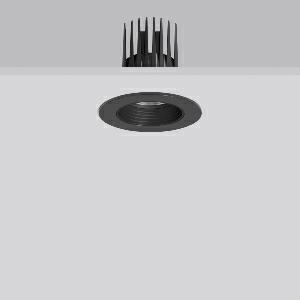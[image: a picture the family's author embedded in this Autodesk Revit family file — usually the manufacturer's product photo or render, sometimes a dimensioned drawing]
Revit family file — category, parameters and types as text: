
# Revit family: heledon_mini_e_901752_003_3_76_12fb
name_source: partatom
category: Lighting Fixtures
units: mm (PartAtom-declared; Revit-internal decimal feet)

## family parameters
Cut with Voids When Loaded = No
Host = Face
Light Source = No
Part Type = Normal
Room Calculation Point = No
Round Connector Dimension = Use Diameter
Shared = No

## types (1)
- HELEDON mini E (1 x LED Modul 935, 3050 lm, 3500)
    Apparent Load = 29 VA
    Approval mark = CE
    CIE Flux Codes = 96 100 100 100 100
    Color Rendering = 92
    Color Temperature = 3500
    Default Elevation = 1800 mm
    Description = Series: HELEDON mini
Round recessed downlight. Housing: die-cast aluminium, powder-coated. Black plastic ring and recessed LED to prevent glare from the side. Optical assembly with lens made of plastic (polycarbonate) for the best homogeneous light distribution - can be changed without tools. Best colour rendering index Ra>90. Suitable for Recessed ceiling mounting. Installation without tools thanks to spring fastening system. Including separate LED converter with connecting cable 600 mm.High quality converter without flickering and stroboscopic effect. Through-wiring box (5 pole) available as accessory. The following accessories can be mounted without use of tools: interchangeable lenses, decorative glasses, honeycomb louvre, clear and frosted diffusers, white interchangeable plastic ring. 
Colour: deep black, matt (RAL 9005)
Diameter: 124 mm
Height: 3 mm
Cut-out diameter: 114 mm
Recess height: 170 mm
Luminaire: recess height: 120 mm
Lamp: LED
Socket: without socket
Colour temperature: 3500K
Colour rendering index (CRI): 92
System power: 29 W
Rated luminous flux: 3050 lm
Luminous efficiency: 105 lm/W
Control gear: Converter, dimmable, DALI
Protection class: II
Type of protection: IP 20
    Height = 0 mm  [stored 0 ft]
    Lamp = 1 x LED Modul 935
    Lamp Light Flux = 3050 lm
    Lamp count = 1
    Length = 124 mm  [stored 0.406824 ft]
    Lifetime = 50000 h
    Luminous efficacy = 105 lm/W
    Manufacturer = RZB
    ModVariant = No
    Model = 901752.003.3.76
    Mounting Place = Ceiling
    Mounting Type = Recessed
    Number of Poles = 1
    OnlyDefault = Yes
    Power Factor = 1
    Product Name = HELEDON mini E
    Product group = Recessed downlights
    ProductGroupID = 402
    Protection Class = Protection class II
    Protection Degree = IP 20
    RLX_Detail_Level = 1
    RLX_Emergency_Light_Flux = 0 lm
    RLX_Emergency_Type = 0
    RLX_Emergency_Type_DB = No
    RlxData = <blob elided: 126937 chars, md5=22338b3a>
    Socket = socket
    Standby Power = 0 W
    System Light Flux = 3050 lm
    System Power = 29 W
    Type Comments = Product without accessories
    Type Image = 901656.003.jpg
    URL = http://relux.com
    VarID = ---
    Voltage = 230 V
    Voltage Range = 220-240 V
    Weight = 0.00 kg
    Width = 0 mm  [stored 0 ft]

note: [stored X ft] marks values corroborated as IEEE doubles in the binary element streams (Revit-internal decimal feet)

## geometry (parser evidence)
native form markers: Blend x4, Sweep x10
no freeform markers — native parametric forms only
